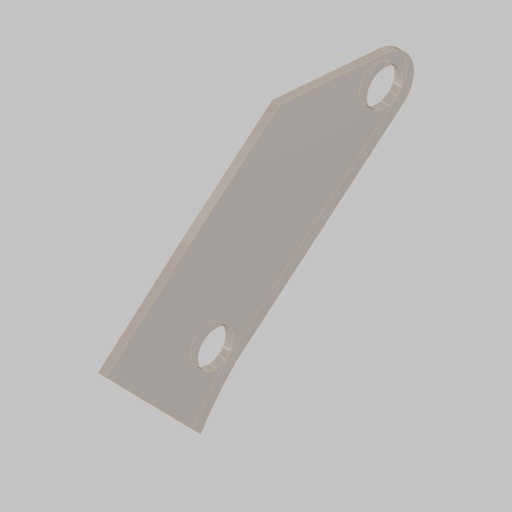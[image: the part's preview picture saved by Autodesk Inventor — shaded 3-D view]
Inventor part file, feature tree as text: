
AUTODESK INVENTOR PART (.ipt)
format: ipt  version: 2023.5 (Build 275446000, 446)  size: 159,232 bytes
history: native  units: in
note: dims shown in document units (in); Inventor stores cm internally (conversion verified against a paired STEP export)
features: sketch x4, extrude x2, hole x1, projected_geometry x1
ambient origin geometry x8: Origin, YZ Plane, XZ Plane, XY Plane, X Axis, Y Axis, Z Axis, Center Point
bodies: Body1 (feature_tree)
feature tree (8):
  sketch  "Sketch1"  dims[d0=16.0in d1=3.0in]
  extrude  "Extrusion2"  Depth=3.0in
  hole  "Hole2"  [1 undecoded]
  extrude  "Extrusion3"  Depth=7.0in
  sketch  "Sketch4"  dims[d2=0.25in d4=4.5in]
  sketch  "Sketch5"  dims[d5=11.875in d6=7.0in]
  sketch  "Sketch6"  dims[d27=1.125in d29=0.375in d31=4.0in d33=4.0in d35=3.75in d36=0.25in d37=0.0in d39=0.5in d41=0.201in d42=0.75in d43=0.385in d44=0.25in d45=0.5635in d46=1.0in d47=0.8108in d51=6.5in d52=11.0in d53=1.2075in d57=1.0in d58=11.75in d59=12.75in d60=1.25in d62=1.0in d63=0.0in]
  projected_geometry  "Projected Loop1"
note: 1 required parameter value undecoded (feature->parameter linkage not recoverable at this tier; creation-order binding heuristic only, values carry confidence <= 0.55)
